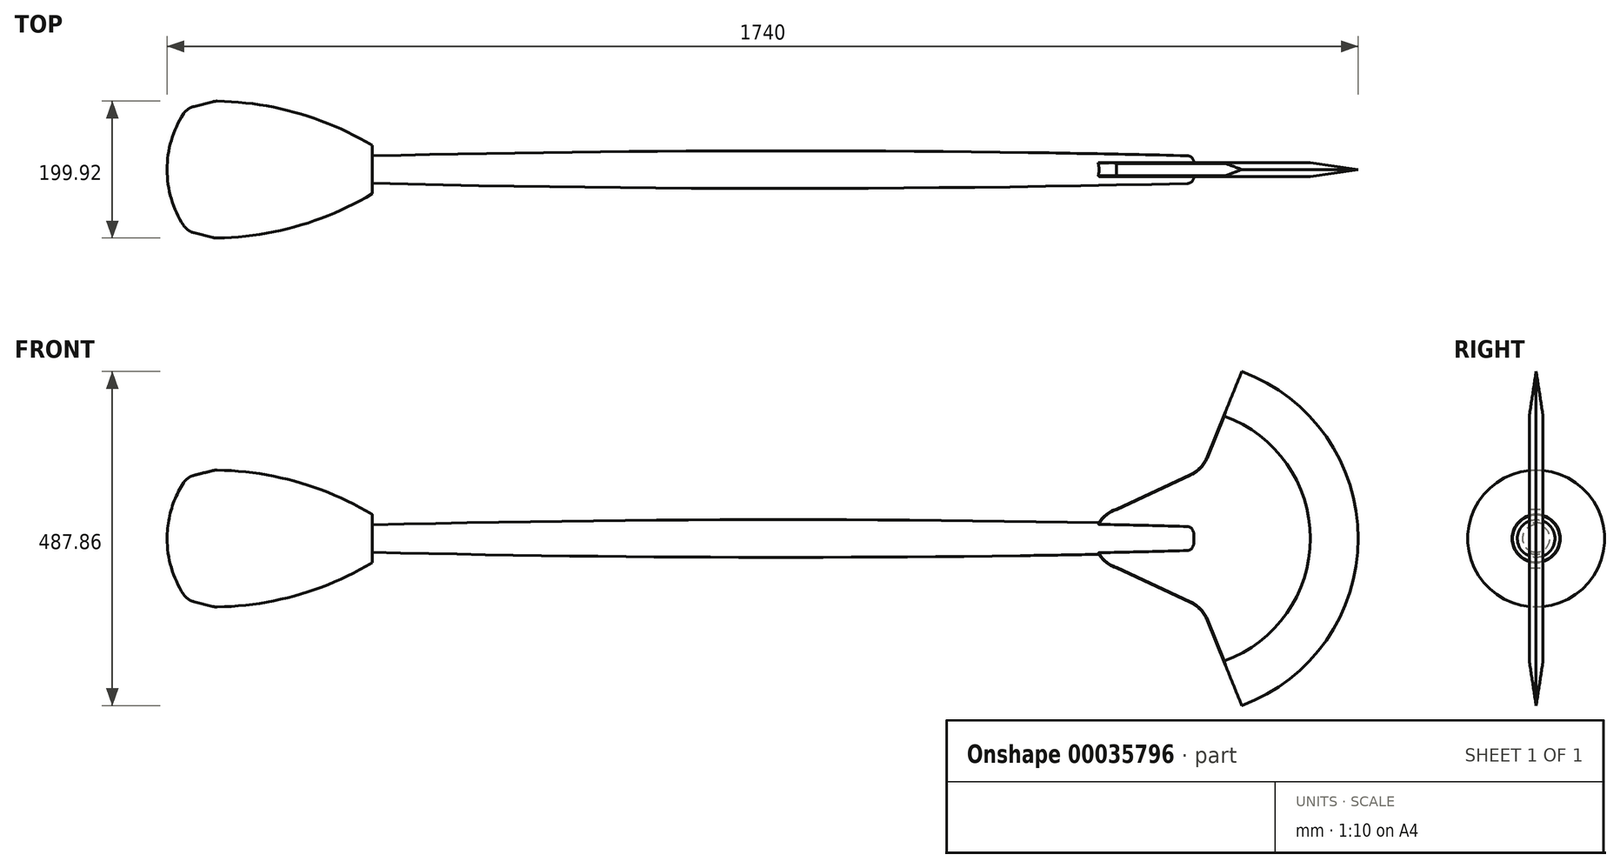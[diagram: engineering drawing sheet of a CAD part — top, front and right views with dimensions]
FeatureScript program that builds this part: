
annotation { "Feature Type Name" : "Feature", "Feature Type Description" : "" }
export const myFeature = defineFeature(function(context is Context, id is Id, definition is map)
    precondition{}
    {
        {
            var Q0;
            Q0=qCreatedBy(makeId("Front.planeOp"),FACE);
            var sketch = newSketch(context, id + "F0", { "sketchPlane" : qUnion([Q0])});
            skLineSegment(sketch, "E0", {"start": v(0, 0) * mm, "end": v(-300, 0) * mm});
            skArc(sketch, "E1", {"start": v(0, 35) * mm, "mid": v(-110.66, 82.87) * mm, "end": v(-230, 100) * mm});
            skLineSegment(sketch, "E2", {"start": v(-230, 100) * mm, "end": v(-270, 90) * mm});
            skArc(sketch, "E3", {"start": v(-270, 90) * mm, "mid": v(-292.3, 47.43) * mm, "end": v(-300, 0) * mm});
            skLineSegment(sketch, "E4", {"start": v(0, 0) * mm, "end": v(0, 35) * mm});
            skLineSegment(sketch, "E5", {"start": v(-300, 0) * mm, "end": v(-300, 191.11) * mm, "construction": true});
            skSolve(sketch);
        }
        {
            var Q0;
            Q0 = qSketchRegion(id + "F0", true);
            var Q1;
            Q1=sQuery(id+"F0.wireOp",EDGE,"E0");
            revolve(context, id + "F1", {"entities" : qUnion([Q0]), "axis" : qUnion([Q1]), "revolveType" : RevolveType.FULL});
        }
        {
            var Q0;
            Q0=makeQuery(id+"F1.opRevolve","SWEPT_EDGE",EDGE,{"disambiguationData":[OSD([sQuery(id+"F0.wireOp",EDGE,"E2"),sQuery(id+"F0.wireOp",EDGE,"E3")])]});
            var Q1;
            Q1=makeQuery(id+"F1.opRevolve","SWEPT_EDGE",EDGE,{"disambiguationData":[OSD([sQuery(id+"F0.wireOp",EDGE,"E1"),sQuery(id+"F0.wireOp",EDGE,"E2")])]});
            fillet(context, id + "F2", {"entities" : qUnion([Q0, Q1]), "radius" : 25 * mm, "tangentPropagation" : true, "allowEdgeOverflow" : false});
        }
        {
            var Q0;
            Q0=qCreatedBy(makeId("Front.planeOp"),FACE);
            var sketch = newSketch(context, id + "F3", { "sketchPlane" : qUnion([Q0])});
            skLineSegment(sketch, "E6", {"start": v(0, 0) * mm, "end": v(1200, 0) * mm});
            skArc(sketch, "E7", {"start": v(1200, 20) * mm, "mid": v(600, 27.5) * mm, "end": v(0, 20) * mm});
            skLineSegment(sketch, "E8", {"start": v(0, 0) * mm, "end": v(0, 20) * mm});
            skLineSegment(sketch, "E9", {"start": v(1200, 0) * mm, "end": v(1200, 20) * mm});
            skSolve(sketch);
        }
        {
            var Q0;
            Q0=makeQuery(id+"F3.imprint","IMPRINT",FACE,{"disambiguationData":[TD([[makeQuery(id+"F3.imprint","IMPRINT",EDGE,{"derivedFrom":sQuery(id+"F3.wireOp",EDGE,"E6")}),1.0]])]});
            var Q1;
            Q1=sQuery(id+"F3.wireOp",EDGE,"E6");
            revolve(context, id + "F4", {"operationType" : NewBodyOperationType.ADD, "entities" : qUnion([Q0]), "axis" : qUnion([Q1]), "revolveType" : RevolveType.FULL});
        }
        {
            var Q0;
            Q0=makeQuery(id+"F4.opRevolve","SWEPT_EDGE",EDGE,{"disambiguationData":[OSD([sQuery(id+"F3.wireOp",EDGE,"E7"),sQuery(id+"F3.wireOp",EDGE,"E9")])]});
            fillet(context, id + "F5", {"entities" : qUnion([Q0]), "radius" : 10 * mm, "tangentPropagation" : true, "allowEdgeOverflow" : false});
        }
        {
            var Q0;
            Q0=qCreatedBy(makeId("Front.planeOp"),FACE);
            var sketch = newSketch(context, id + "F6", { "sketchPlane" : qUnion([Q0])});
            skLineSegment(sketch, "E10", {"start": v(0, 0) * mm, "end": v(1100, 0) * mm, "construction": true});
            skArc(sketch, "E11", {"start": v(1086.83, 43.03) * mm, "mid": v(1055, 0) * mm, "end": v(1086.83, -43.03) * mm});
            skLineSegment(sketch, "E12", {"start": v(1086.83, 43.03) * mm, "end": v(1194.34, 93.16) * mm});
            skLineSegment(sketch, "E13", {"start": v(1219.54, 119.67) * mm, "end": v(1270, 243.93) * mm});
            skLineSegment(sketch, "E14.MirrorCS", {"start": v(1086.83, -43.03) * mm, "end": v(1194.34, -93.16) * mm});
            skLineSegment(sketch, "E15.MirrorCS", {"start": v(1219.54, -119.67) * mm, "end": v(1270, -243.93) * mm});
            skArc(sketch, "E16", {"start": v(1270, -243.93) * mm, "mid": v(1440, 0) * mm, "end": v(1270, 243.93) * mm});
            skPoint(sketch, "E17.orphan", {"position": v(1305.05, -330.24) * mm});
            skPoint(sketch, "E18.orphan", {"position": v(1305.05, 330.24) * mm});
            skPoint(sketch, "E19.visualSharp", {"position": v(1212.15, 101.47) * mm});
            skArc(sketch, "E19.filletArc", {"start": v(1194.34, 93.16) * mm, "mid": v(1209.45, 104.03) * mm, "end": v(1219.54, 119.67) * mm});
            skPoint(sketch, "E20.visualSharp", {"position": v(1212.15, -101.47) * mm});
            skArc(sketch, "E20.filletArc", {"start": v(1219.54, -119.67) * mm, "mid": v(1209.45, -104.03) * mm, "end": v(1194.34, -93.16) * mm});
            skSolve(sketch);
        }
        {
            var Q0;
            Q0=makeQuery(id+"F6.imprint","IMPRINT",FACE,{"disambiguationData":[TD([[makeQuery(id+"F6.imprint","IMPRINT",EDGE,{"derivedFrom":sQuery(id+"F6.wireOp",EDGE,"E11")}),1.0]])]});
            extrude(context, id + "F7", {"entities" : qUnion([Q0]), "operationType" : NewBodyOperationType.ADD, "depth" : 20 * mm, "symmetric" : true});
        }
        {
            var Q0;
            Q0=makeQuery(id+"F7.opExtrude","CAP_EDGE",EDGE,{"disambiguationData":[OSD([sQuery(id+"F6.wireOp",EDGE,"E16")])],"isStart":false});
            chamfer(context, id + "F8", {"entities" : qUnion([Q0]), "chamferType" : ChamferType.TWO_OFFSETS, "width1" : 10 * mm, "oppositeDirection" : true, "width2" : 70 * mm, "tangentPropagation" : true});
        }
        {
            var Q0;
            Q0=makeQuery(id+"F7.opExtrude","CAP_EDGE",EDGE,{"disambiguationData":[OSD([sQuery(id+"F6.wireOp",EDGE,"E16")])],"isStart":true});
            chamfer(context, id + "F9", {"entities" : qUnion([Q0]), "chamferType" : ChamferType.TWO_OFFSETS, "width1" : 10 * mm, "oppositeDirection" : false, "width2" : 70 * mm, "tangentPropagation" : true});
        }
        {
            var Q0;
            Q0=makeQuery(id+"F1.opRevolve","SWEPT_EDGE",EDGE,{"disambiguationData":[OSD([sQuery(id+"F0.wireOp",EDGE,"E1"),sQuery(id+"F0.wireOp",EDGE,"E4")])]});
            var Q1;
            Q1=makeQuery(id+"F7.opExtrude","CAP_EDGE",EDGE,{"disambiguationData":[OSD([sQuery(id+"F6.wireOp",EDGE,"E14.MirrorCS")])],"isStart":true});
            var Q2;
            {var subQ0=sQuery(id+"F6.wireOp",EDGE,"E11");var subQ1=sQuery(id+"F6.wireOp",EDGE,"E14.MirrorCS");Q2=makeQuery(id+"F7.boolean.opBoolean","SPLIT",EDGE,{"disambiguationData":[TD([makeQuery(id+"F7.opExtrude","SWEPT_FACE",FACE,{"disambiguationData":[OSD([subQ1])]})])],"derivedFrom":makeQuery(id+"F7.opExtrude","CAP_EDGE",EDGE,{"disambiguationData":[OSD([subQ0])],"isStart":true})});}
            var Q3;
            Q3=makeQuery(id+"F7.opExtrude","CAP_EDGE",EDGE,{"disambiguationData":[OSD([sQuery(id+"F6.wireOp",EDGE,"E12")])],"isStart":true});
            var Q4;
            Q4=makeQuery(id+"F7.opExtrude","CAP_EDGE",EDGE,{"disambiguationData":[OSD([sQuery(id+"F6.wireOp",EDGE,"E14.MirrorCS")])],"isStart":false});
            var Q5;
            Q5=makeQuery(id+"F7.opExtrude","CAP_EDGE",EDGE,{"disambiguationData":[OSD([sQuery(id+"F6.wireOp",EDGE,"E12")])],"isStart":false});
            var Q6;
            {var subQ0=sQuery(id+"F6.wireOp",EDGE,"E11");var subQ1=sQuery(id+"F6.wireOp",EDGE,"E14.MirrorCS");Q6=makeQuery(id+"F7.boolean.opBoolean","SPLIT",EDGE,{"disambiguationData":[TD([makeQuery(id+"F7.opExtrude","SWEPT_FACE",FACE,{"disambiguationData":[OSD([subQ1])]})])],"derivedFrom":makeQuery(id+"F7.opExtrude","CAP_EDGE",EDGE,{"disambiguationData":[OSD([subQ0])],"isStart":false})});}
            var Q7;
            {var subQ0=sQuery(id+"F6.wireOp",EDGE,"E11");var subQ1=sQuery(id+"F6.wireOp",EDGE,"E12");Q7=makeQuery(id+"F7.boolean.opBoolean","SPLIT",EDGE,{"disambiguationData":[TD([makeQuery(id+"F7.opExtrude","SWEPT_FACE",FACE,{"disambiguationData":[OSD([subQ1])]})])],"derivedFrom":makeQuery(id+"F7.opExtrude","CAP_EDGE",EDGE,{"disambiguationData":[OSD([subQ0])],"isStart":false})});}
            var Q8;
            Q8=makeQuery(id+"F7.opExtrude","CAP_EDGE",EDGE,{"disambiguationData":[OSD([sQuery(id+"F6.wireOp",EDGE,"E19.filletArc")])],"isStart":false});
            var Q9;
            Q9=makeQuery(id+"F7.opExtrude","CAP_EDGE",EDGE,{"disambiguationData":[OSD([sQuery(id+"F6.wireOp",EDGE,"E13")])],"isStart":false});
            chamfer(context, id + "F10", {"entities" : qUnion([Q0, Q1, Q2, Q3, Q4, Q5, Q6, Q7, Q8, Q9]), "width" : 1 * mm, "tangentPropagation" : true});
        }
    });
